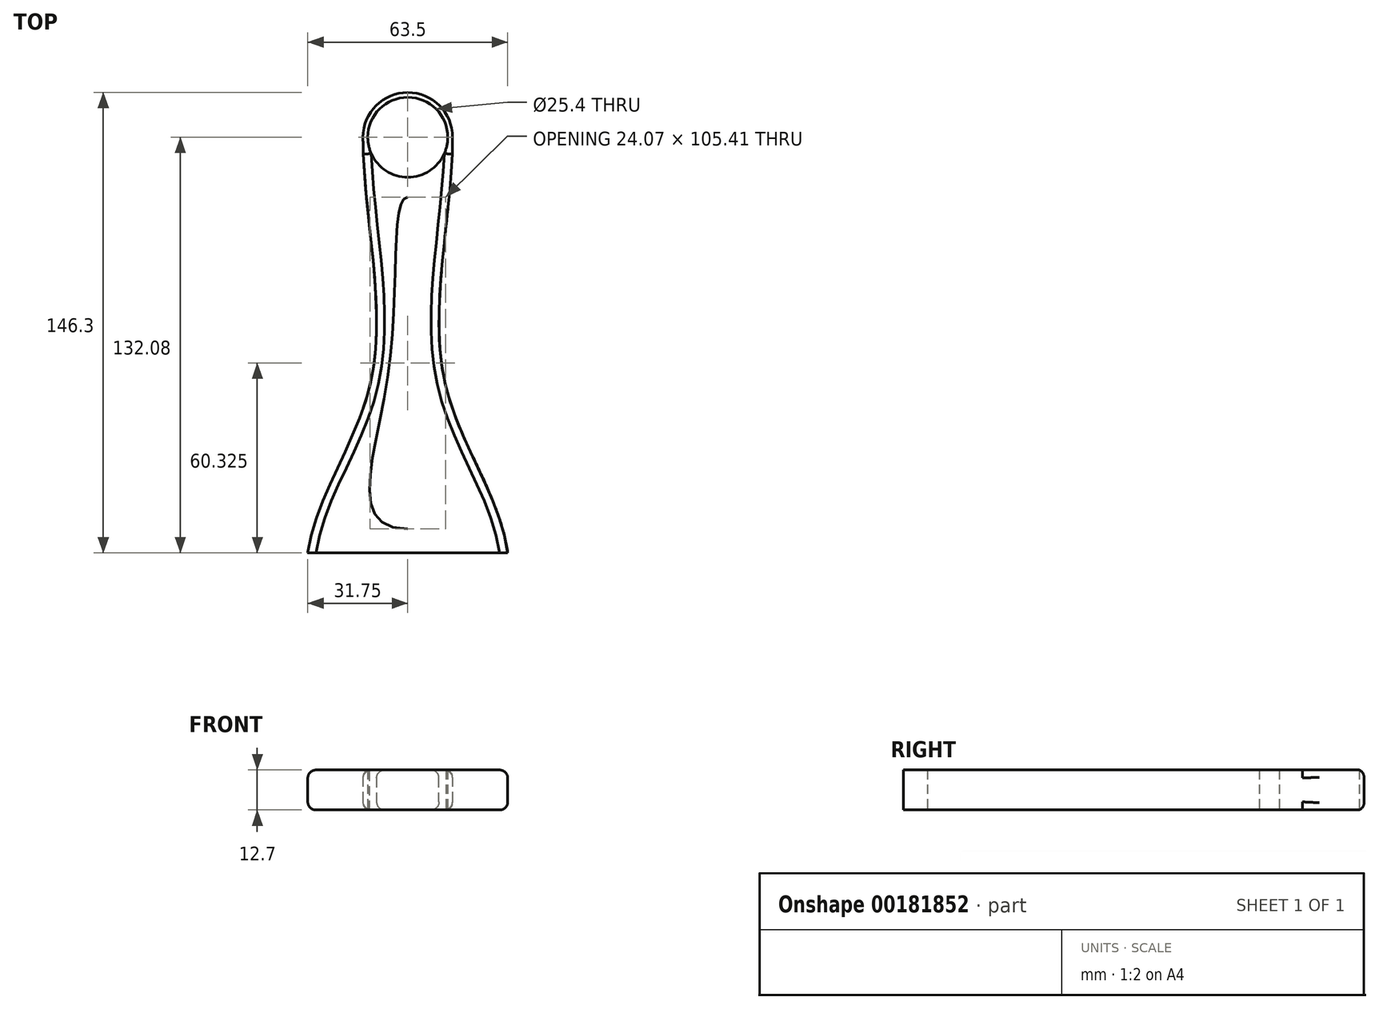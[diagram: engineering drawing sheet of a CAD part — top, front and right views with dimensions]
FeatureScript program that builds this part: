
annotation { "Feature Type Name" : "Feature", "Feature Type Description" : "" }
export const myFeature = defineFeature(function(context is Context, id is Id, definition is map)
    precondition{}
    {
        {
            var Q0;
            Q0=qCreatedBy(makeId("Top.planeOp"),FACE);
            var sketch = newSketch(context, id + "F0", { "sketchPlane" : qUnion([Q0])});
            skCircle(sketch, "E0", {"center": v(0, 76.2) * mm, "radius": 14.22 * mm});
            skFitSpline(sketch, "E1", {"points": [v(-14.22, 76.2) * mm, v(-11.43, 0) * mm, v(-31.75, -55.88) * mm], "startDerivative": vector(0, -136.2) * mm, "endDerivative": vector(-17.77, -123.8) * mm});
            skFitSpline(sketch, "E2.MirrorCS", {"points": [v(14.22, 76.2) * mm, v(11.43, 0) * mm, v(31.75, -55.88) * mm], "startDerivative": vector(0, -136.2) * mm, "endDerivative": vector(17.77, -123.8) * mm});
            skCircle(sketch, "E3.0", {"center": v(0, 76.2) * mm, "radius": 12.7 * mm});
            skFitSpline(sketch, "E4", {"points": [v(0, 57.15) * mm, v(-6.35, 0) * mm, v(0, -48.26) * mm], "startDerivative": vector(-33.3, 0) * mm, "endDerivative": vector(125.98, 0) * mm});
            skFitSpline(sketch, "E5.MirrorCS", {"points": [v(0, 57.15) * mm, v(6.35, 0) * mm, v(0, -48.26) * mm], "startDerivative": vector(33.3, 0) * mm, "endDerivative": vector(-125.98, 0) * mm});
            skLineSegment(sketch, "E6", {"start": v(-31.75, -55.88) * mm, "end": v(0, -55.88) * mm});
            skLineSegment(sketch, "E7.MirrorCS", {"start": v(31.75, -55.88) * mm, "end": v(0, -55.88) * mm});
            skSolve(sketch);
        }
        {
            var Q0;
            Q0 = qSketchRegion(id + "F0", true);
            extrude(context, id + "F1", {"entities" : qUnion([Q0]), "depth" : 12.7 * mm, "symmetric" : true});
        }
        {
            var Q0;
            Q0=makeQuery(id+"F1.opExtrude","CAP_EDGE",EDGE,{"disambiguationData":[OSD([sQuery(id+"F0.wireOp",EDGE,"E1")])],"isStart":false});
            var Q1;
            Q1=makeQuery(id+"F1.opExtrude","CAP_EDGE",EDGE,{"disambiguationData":[OSD([sQuery(id+"F0.wireOp",EDGE,"E1")])],"isStart":true});
            var Q2;
            Q2=makeQuery(id+"F1.opExtrude","CAP_EDGE",EDGE,{"disambiguationData":[OSD([sQuery(id+"F0.wireOp",EDGE,"E0")])],"isStart":false});
            var Q3;
            Q3=makeQuery(id+"F1.opExtrude","CAP_EDGE",EDGE,{"disambiguationData":[OSD([sQuery(id+"F0.wireOp",EDGE,"E0")])],"isStart":true});
            var Q4;
            Q4=makeQuery(id+"F1.opExtrude","CAP_EDGE",EDGE,{"disambiguationData":[OSD([sQuery(id+"F0.wireOp",EDGE,"E2.MirrorCS")])],"isStart":false});
            var Q5;
            Q5=makeQuery(id+"F1.opExtrude","CAP_EDGE",EDGE,{"disambiguationData":[OSD([sQuery(id+"F0.wireOp",EDGE,"E2.MirrorCS")])],"isStart":true});
            fillet(context, id + "F2", {"entities" : qUnion([Q0, Q1, Q2, Q3, Q4, Q5]), "radius" : 2.54 * mm, "tangentPropagation" : true, "allowEdgeOverflow" : false});
        }
    });
